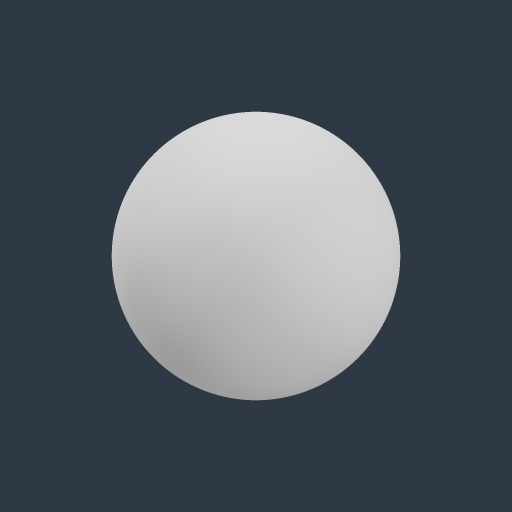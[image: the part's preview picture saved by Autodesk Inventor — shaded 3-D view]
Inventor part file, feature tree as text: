
AUTODESK INVENTOR PART (.ipt)
format: ipt  version: 2024.3 (Build 283343000, 343)  size: 122,880 bytes
history: native  units: in
note: dims shown in document units (in); Inventor stores cm internally (conversion verified against a paired STEP export)
features: revolve x1, sketch x1
ambient origin geometry x8: Origin, YZ Plane, XZ Plane, XY Plane, X Axis, Y Axis, Z Axis, Center Point
bodies: Solid1 (feature_tree)
feature tree (2):
  revolve  "Revolution1"  [1 undecoded]
  sketch  "Sketch1"  dims[d0=16.0in d1=16.0in d2=90.0deg]
note: 1 required parameter value undecoded (feature->parameter linkage not recoverable at this tier; creation-order binding heuristic only, values carry confidence <= 0.55)
